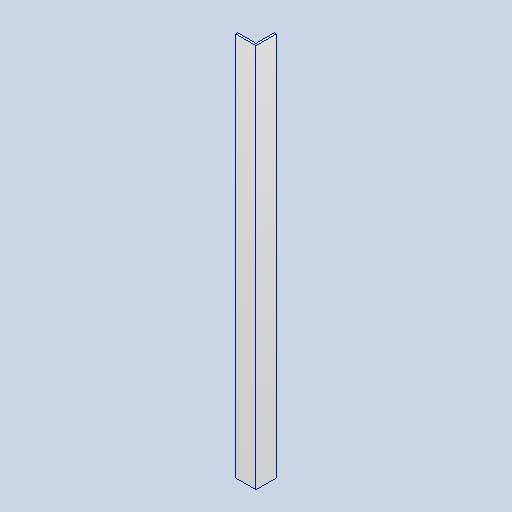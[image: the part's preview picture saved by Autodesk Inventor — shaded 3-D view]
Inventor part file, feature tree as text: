
AUTODESK INVENTOR PART (.ipt)
format: ipt  version: 2022 (Build 260153000, 153)  size: 99,840 bytes
history: native  units: mm
features: extrude x1, sketch x1
ambient origin geometry x8: Origin, YZ Plane, XZ Plane, XY Plane, X Axis, Y Axis, Z Axis, Center Point
bodies: Solid1 (feature_tree)
feature tree (2):
  extrude  "Extrusion1"  Depth=50.0mm
  sketch  "Sketch1"  dims[d0=50.0mm d1=50.0mm d2=5.0mm d3=5.0mm d4=950.0mm d5=0.0mm]
